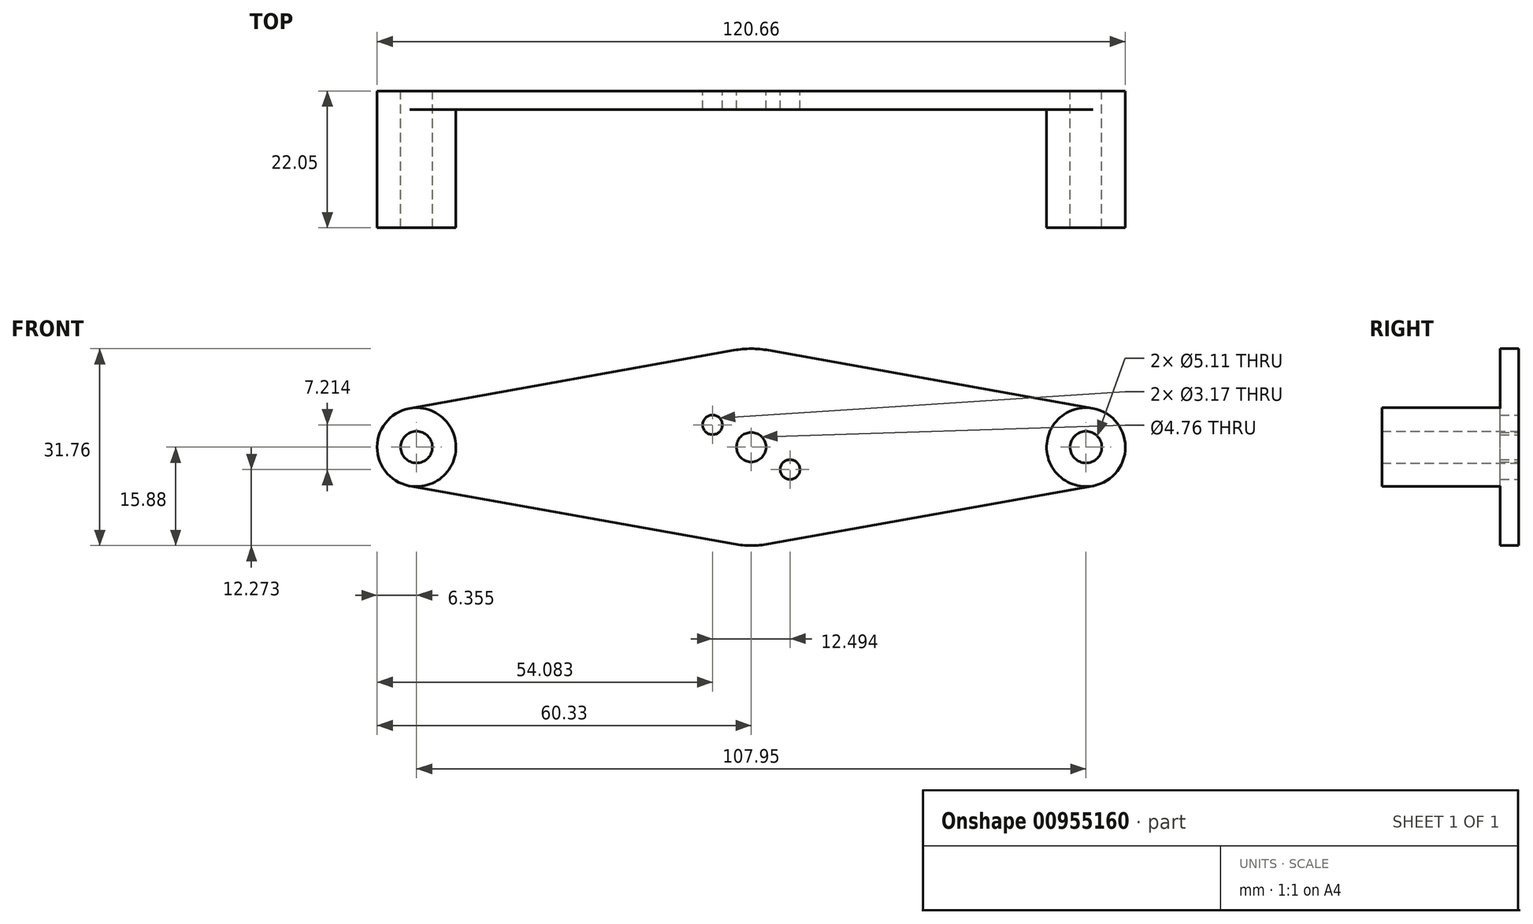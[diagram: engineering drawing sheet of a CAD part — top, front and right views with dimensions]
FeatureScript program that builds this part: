
annotation { "Feature Type Name" : "Feature", "Feature Type Description" : "" }
export const myFeature = defineFeature(function(context is Context, id is Id, definition is map)
    precondition{}
    {
        {
            var Q0;
            Q0=qCreatedBy(makeId("Front.planeOp"),FACE);
            var sketch = newSketch(context, id + "F0", { "sketchPlane" : qUnion([Q0])});
            skCircle(sketch, "E0", {"center": v(-53.98, 0) * mm, "radius": 2.55 * mm});
            skCircle(sketch, "E1", {"center": v(53.98, 0) * mm, "radius": 2.55 * mm});
            skCircle(sketch, "E2", {"center": v(53.98, 0) * mm, "radius": 6.35 * mm, "construction": true});
            skCircle(sketch, "E3", {"center": v(-53.98, 0) * mm, "radius": 6.35 * mm, "construction": true});
            skLineSegment(sketch, "E4", {"start": v(-53.98, 0) * mm, "end": v(0, 0) * mm, "construction": true});
            skLineSegment(sketch, "E5", {"start": v(53.98, 0) * mm, "end": v(0, 0) * mm, "construction": true});
            skLineSegment(sketch, "E6", {"start": v(-6.25, 3.6) * mm, "end": v(0, 0) * mm, "construction": true});
            skLineSegment(sketch, "E7", {"start": v(0, 0) * mm, "end": v(6.25, -3.6) * mm, "construction": true});
            skCircle(sketch, "E8", {"center": v(-6.25, 3.6) * mm, "radius": 1.59 * mm});
            skCircle(sketch, "E9", {"center": v(6.25, -3.6) * mm, "radius": 1.59 * mm});
            skCircle(sketch, "E10", {"center": v(0, 0) * mm, "radius": 2.38 * mm});
            skCircle(sketch, "E11", {"center": v(0, 0) * mm, "radius": 15.88 * mm, "construction": true});
            skLineSegment(sketch, "E12", {"start": v(-55.1, 6.25) * mm, "end": v(-2.8, 15.63) * mm});
            skLineSegment(sketch, "E13", {"start": v(-55.1, -6.25) * mm, "end": v(-2.8, -15.63) * mm});
            skLineSegment(sketch, "E14", {"start": v(55.1, -6.25) * mm, "end": v(2.8, -15.63) * mm});
            skLineSegment(sketch, "E15", {"start": v(55.1, 6.25) * mm, "end": v(2.8, 15.63) * mm});
            skArc(sketch, "E16", {"start": v(2.8, -15.63) * mm, "mid": v(0, -15.87) * mm, "end": v(-2.8, -15.63) * mm});
            skArc(sketch, "E17", {"start": v(2.8, 15.63) * mm, "mid": v(0, 15.87) * mm, "end": v(-2.8, 15.63) * mm});
            skArc(sketch, "E18", {"start": v(-55.1, 6.25) * mm, "mid": v(-60.33, 0) * mm, "end": v(-55.1, -6.25) * mm});
            skArc(sketch, "E19", {"start": v(55.1, 6.25) * mm, "mid": v(60.32, 0) * mm, "end": v(55.1, -6.25) * mm});
            skSolve(sketch);
        }
        {
            var Q0;
            Q0=qSketchRegion(id+"F0",true);
            extrude(context, id + "F1", {"entities" : qUnion([Q0]), "depth" : 3 * mm, "offsetDistance" : 25.4 * mm});
        }
        {
            var Q0;
            Q0=makeQuery(id+"F1.opExtrude","CAP_FACE",FACE,{"disambiguationData":[OSD([sQuery(id+"F0.wireOp",EDGE,"E0"),sQuery(id+"F0.wireOp",EDGE,"E1"),sQuery(id+"F0.wireOp",EDGE,"E8"),sQuery(id+"F0.wireOp",EDGE,"E9"),sQuery(id+"F0.wireOp",EDGE,"E10"),sQuery(id+"F0.wireOp",EDGE,"E12"),sQuery(id+"F0.wireOp",EDGE,"E13"),sQuery(id+"F0.wireOp",EDGE,"E14"),sQuery(id+"F0.wireOp",EDGE,"E15"),sQuery(id+"F0.wireOp",EDGE,"E16"),sQuery(id+"F0.wireOp",EDGE,"E17"),sQuery(id+"F0.wireOp",EDGE,"E18"),sQuery(id+"F0.wireOp",EDGE,"E19")])],"isStart":false});
            var sketch = newSketch(context, id + "F2", { "sketchPlane" : qUnion([Q0])});
            skCircle(sketch, "E20", {"center": v(-53.98, 0) * mm, "radius": 2.55 * mm});
            skCircle(sketch, "E21", {"center": v(53.98, 0) * mm, "radius": 2.55 * mm});
            skCircle(sketch, "E22", {"center": v(53.98, 0) * mm, "radius": 6.35 * mm});
            skCircle(sketch, "E23", {"center": v(-53.98, 0) * mm, "radius": 6.35 * mm});
            skSolve(sketch);
        }
        {
            var Q0;
            Q0=qSketchRegion(id+"F2",true);
            extrude(context, id + "F3", {"entities" : qUnion([Q0]), "operationType" : NewBodyOperationType.ADD, "depth" : 19.05 * mm, "offsetDistance" : 25.4 * mm});
        }
    });
